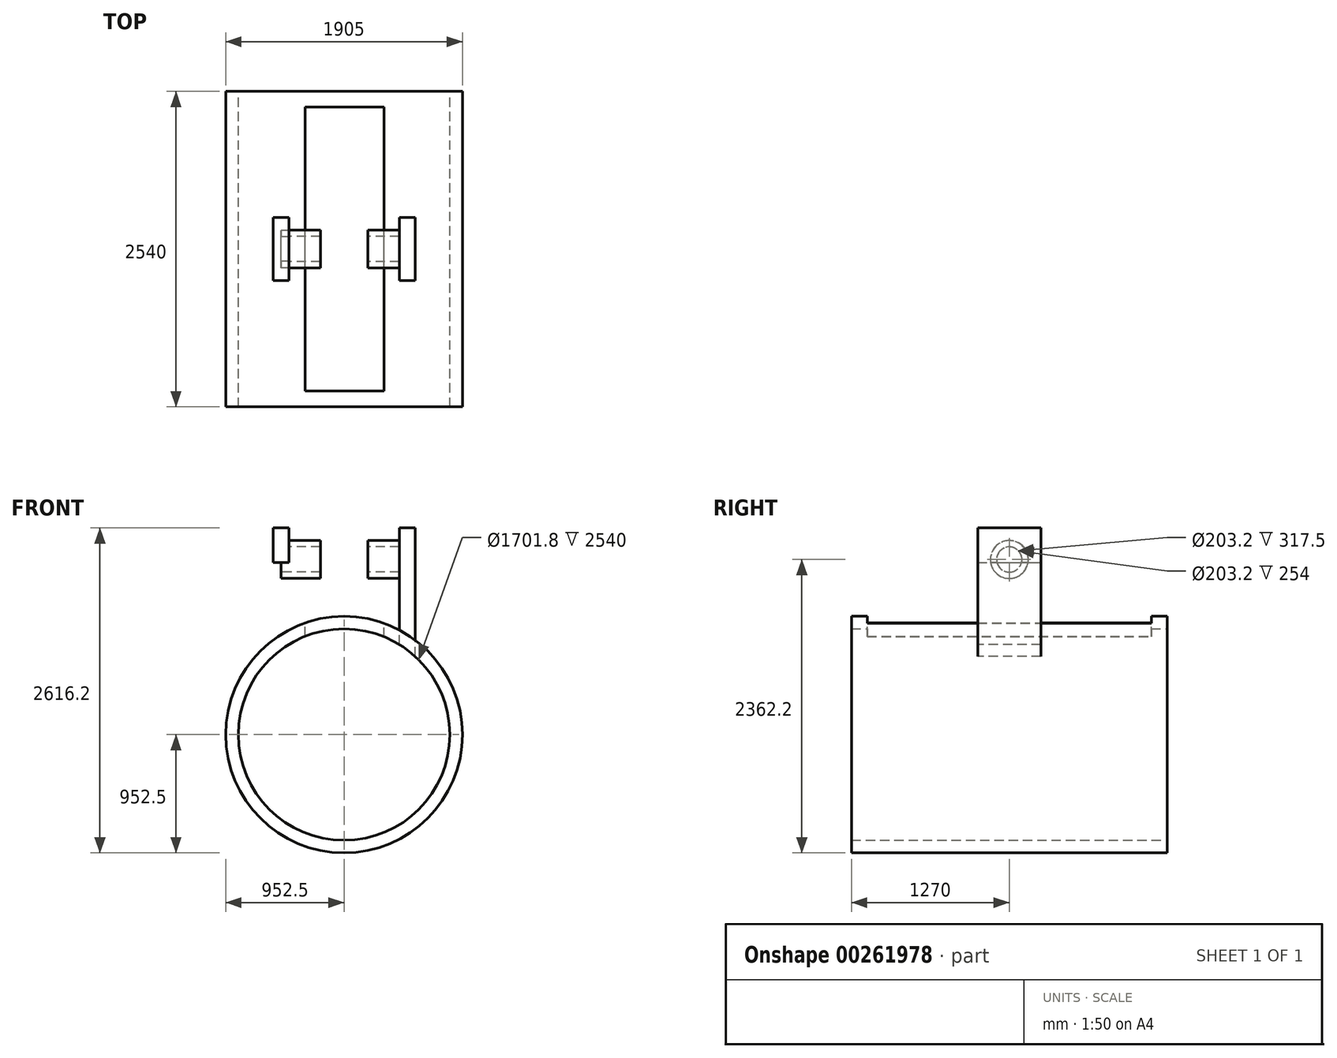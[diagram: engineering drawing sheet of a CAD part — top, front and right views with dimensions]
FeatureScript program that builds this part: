
annotation { "Feature Type Name" : "Feature", "Feature Type Description" : "" }
export const myFeature = defineFeature(function(context is Context, id is Id, definition is map)
    precondition{}
    {
        {
            var Q0;
            Q0=qCreatedBy(makeId("Right.planeOp"),FACE);
            var sketch = newSketch(context, id + "F0", { "sketchPlane" : qUnion([Q0])});
            skCircle(sketch, "E0", {"center": v(0, -114.3) * mm, "radius": 152.4 * mm});
            skCircle(sketch, "E1", {"center": v(0, -114.3) * mm, "radius": 101.6 * mm});
            skSolve(sketch);
        }
        {
            var Q0;
            Q0=makeQuery(id+"F0.imprint","IMPRINT",FACE,{"disambiguationData":[TD([[makeQuery(id+"F0.imprint","IMPRINT",EDGE,{"derivedFrom":sQuery(id+"F0.wireOp",EDGE,"E0")}),1.0]])]});
            extrude(context, id + "F1", {"entities" : qUnion([Q0]), "endBound" : BoundingType.SYMMETRIC, "depth" : 1016 * mm});
        }
        {
            var Q0;
            Q0=makeQuery(id+"F0.imprint","IMPRINT",FACE,{"disambiguationData":[TD([[makeQuery(id+"F0.imprint","IMPRINT",EDGE,{"derivedFrom":sQuery(id+"F0.wireOp",EDGE,"E0")}),1.0]])]});
            extrude(context, id + "F2", {"entities" : qUnion([Q0]), "operationType" : NewBodyOperationType.REMOVE, "endBound" : BoundingType.SYMMETRIC, "oppositeDirection" : true, "depth" : 381 * mm});
        }
        {
            var Q0;
            Q0=qCreatedBy(makeId("Right.planeOp"),FACE);
            cPlane(context, id + "F3", {"entities" : qUnion([Q0]), "cplaneType" : CPlaneType.OFFSET, "offset" : 508 * mm, "width" : 152.4 * mm, "height" : 152.4 * mm});
        }
        {
            var Q0;
            Q0=qCreatedBy(id+"F3.planeOp",FACE);
            var sketch = newSketch(context, id + "F4", { "sketchPlane" : qUnion([Q0])});
            skLineSegment(sketch, "E2.bottom", {"start": v(254, -368.3) * mm, "end": v(-254, -368.3) * mm});
            skLineSegment(sketch, "E2.top", {"start": v(254, 139.7) * mm, "end": v(-254, 139.7) * mm});
            skLineSegment(sketch, "E2.left", {"start": v(254, -368.3) * mm, "end": v(254, 139.7) * mm});
            skLineSegment(sketch, "E2.right", {"start": v(-254, -368.3) * mm, "end": v(-254, 139.7) * mm});
            skPoint(sketch, "E2.middle", {"position": v(0, -114.3) * mm});
            skLineSegment(sketch, "E3.bottom", {"start": v(-254, -368.3) * mm, "end": v(254, -368.3) * mm});
            skLineSegment(sketch, "E3.top", {"start": v(-254, -1003.3) * mm, "end": v(254, -1003.3) * mm});
            skLineSegment(sketch, "E3.left", {"start": v(-254, -368.3) * mm, "end": v(-254, -1003.3) * mm});
            skLineSegment(sketch, "E3.right", {"start": v(254, -368.3) * mm, "end": v(254, -1003.3) * mm});
            skSolve(sketch);
        }
        {
            var Q0;
            Q0=qCreatedBy(makeId("Front.planeOp"),FACE);
            var sketch = newSketch(context, id + "F5", { "sketchPlane" : qUnion([Q0])});
            skCircle(sketch, "E4", {"center": v(0, -1524) * mm, "radius": 952.5 * mm});
            skCircle(sketch, "E5", {"center": v(0, -1524) * mm, "radius": 850.9 * mm});
            skSolve(sketch);
        }
        {
            var Q0;
            Q0=qSketchRegion(id+"F4",true);
            extrude(context, id + "F6", {"entities" : qUnion([Q0]), "operationType" : NewBodyOperationType.ADD, "endBound" : BoundingType.SYMMETRIC, "depth" : 127 * mm});
        }
        {
            var Q0;
            Q0=qCreatedBy(makeId("Right.planeOp"),FACE);
            cPlane(context, id + "F7", {"entities" : qUnion([Q0]), "cplaneType" : CPlaneType.OFFSET, "offset" : 508 * mm, "oppositeDirection" : true, "width" : 152.4 * mm, "height" : 152.4 * mm});
        }
        {
            var Q0;
            Q0=qCreatedBy(id+"F7.planeOp",FACE);
            var sketch = newSketch(context, id + "F8", { "sketchPlane" : qUnion([Q0])});
            skLineSegment(sketch, "E6.bottom", {"start": v(-254, -139.7) * mm, "end": v(254, -139.7) * mm});
            skLineSegment(sketch, "E6.top", {"start": v(-254, 139.7) * mm, "end": v(254, 139.7) * mm});
            skLineSegment(sketch, "E6.left", {"start": v(-254, -139.7) * mm, "end": v(-254, 139.7) * mm});
            skLineSegment(sketch, "E6.right", {"start": v(254, -139.7) * mm, "end": v(254, 139.7) * mm});
            skPoint(sketch, "E6.middle", {"position": v(0, 0) * mm});
            skLineSegment(sketch, "E7.bottom", {"start": v(254, -139.7) * mm, "end": v(-254, -139.7) * mm});
            skLineSegment(sketch, "E7.top", {"start": v(254, -1003.3) * mm, "end": v(-254, -1003.3) * mm});
            skLineSegment(sketch, "E7.left", {"start": v(254, -139.7) * mm, "end": v(254, -1003.3) * mm});
            skLineSegment(sketch, "E7.right", {"start": v(-254, -139.7) * mm, "end": v(-254, -1003.3) * mm});
            skSolve(sketch);
        }
        {
            var Q0;
            Q0=makeQuery(id+"F8.imprint","IMPRINT",FACE,{"disambiguationData":[TD([[makeQuery(id+"F8.imprint","IMPRINT",EDGE,{"derivedFrom":sQuery(id+"F8.wireOp",EDGE,"E7.bottom")}),1.0]])]});
            var Q1;
            Q1=makeQuery(id+"F8.imprint","IMPRINT",FACE,{"disambiguationData":[TD([[makeQuery(id+"F8.imprint","IMPRINT",EDGE,{"derivedFrom":sQuery(id+"F8.wireOp",EDGE,"E6.top")}),-1.0]])]});
            extrude(context, id + "F9", {"entities" : qUnion([Q0, Q1]), "operationType" : NewBodyOperationType.ADD, "endBound" : BoundingType.SYMMETRIC, "depth" : 127 * mm});
        }
        {
            var Q0;
            Q0=makeQuery(id+"F5.imprint","IMPRINT",FACE,{"disambiguationData":[TD([[makeQuery(id+"F5.imprint","IMPRINT",EDGE,{"derivedFrom":sQuery(id+"F5.wireOp",EDGE,"E4")}),1.0]])]});
            extrude(context, id + "F10", {"entities" : qUnion([Q0]), "endBound" : BoundingType.SYMMETRIC, "depth" : 2540 * mm});
        }
        {
            var Q0;
            Q0=makeQuery(id+"F5.imprint","IMPRINT",FACE,{"disambiguationData":[TD([[makeQuery(id+"F5.imprint","IMPRINT",EDGE,{"derivedFrom":sQuery(id+"F5.wireOp",EDGE,"E5")}),1.0]])]});
            extrude(context, id + "F11", {"entities" : qUnion([Q0]), "operationType" : NewBodyOperationType.REMOVE, "endBound" : BoundingType.THROUGH_ALL, "oppositeDirection" : true, "depth" : 25.4 * mm});
        }
        {
            var Q0;
            Q0=makeQuery(id+"F5.imprint","IMPRINT",FACE,{"disambiguationData":[TD([[makeQuery(id+"F5.imprint","IMPRINT",EDGE,{"derivedFrom":sQuery(id+"F5.wireOp",EDGE,"E5")}),1.0]])]});
            extrude(context, id + "F12", {"entities" : qUnion([Q0]), "operationType" : NewBodyOperationType.REMOVE, "endBound" : BoundingType.THROUGH_ALL, "depth" : 25.4 * mm});
        }
        {
            var Q0;
            Q0=qCreatedBy(makeId("Top.planeOp"),FACE);
            cPlane(context, id + "F13", {"entities" : qUnion([Q0]), "cplaneType" : CPlaneType.OFFSET, "offset" : 381 * mm, "oppositeDirection" : true, "width" : 152.4 * mm, "height" : 152.4 * mm});
        }
        {
            var Q0;
            Q0=qCreatedBy(id+"F13.planeOp",FACE);
            var sketch = newSketch(context, id + "F14", { "sketchPlane" : qUnion([Q0])});
            skLineSegment(sketch, "E8.bottom", {"start": v(323.16, -1143) * mm, "end": v(-311.84, -1143) * mm});
            skLineSegment(sketch, "E8.top", {"start": v(323.16, 1143) * mm, "end": v(-311.84, 1143) * mm});
            skLineSegment(sketch, "E8.left", {"start": v(323.16, -1143) * mm, "end": v(323.16, 1143) * mm});
            skLineSegment(sketch, "E8.right", {"start": v(-311.84, -1143) * mm, "end": v(-311.84, 1143) * mm});
            skPoint(sketch, "E8.middle", {"position": v(5.66, 0) * mm});
            skSolve(sketch);
        }
        {
            var Q0;
            Q0=makeQuery(id+"F14.imprint","IMPRINT",FACE,{"disambiguationData":[TD([[makeQuery(id+"F14.imprint","IMPRINT",EDGE,{"derivedFrom":sQuery(id+"F14.wireOp",EDGE,"E8.bottom")}),-1.0]])]});
            extrude(context, id + "F15", {"entities" : qUnion([Q0]), "operationType" : NewBodyOperationType.REMOVE, "oppositeDirection" : true, "depth" : 508 * mm});
        }
    });
